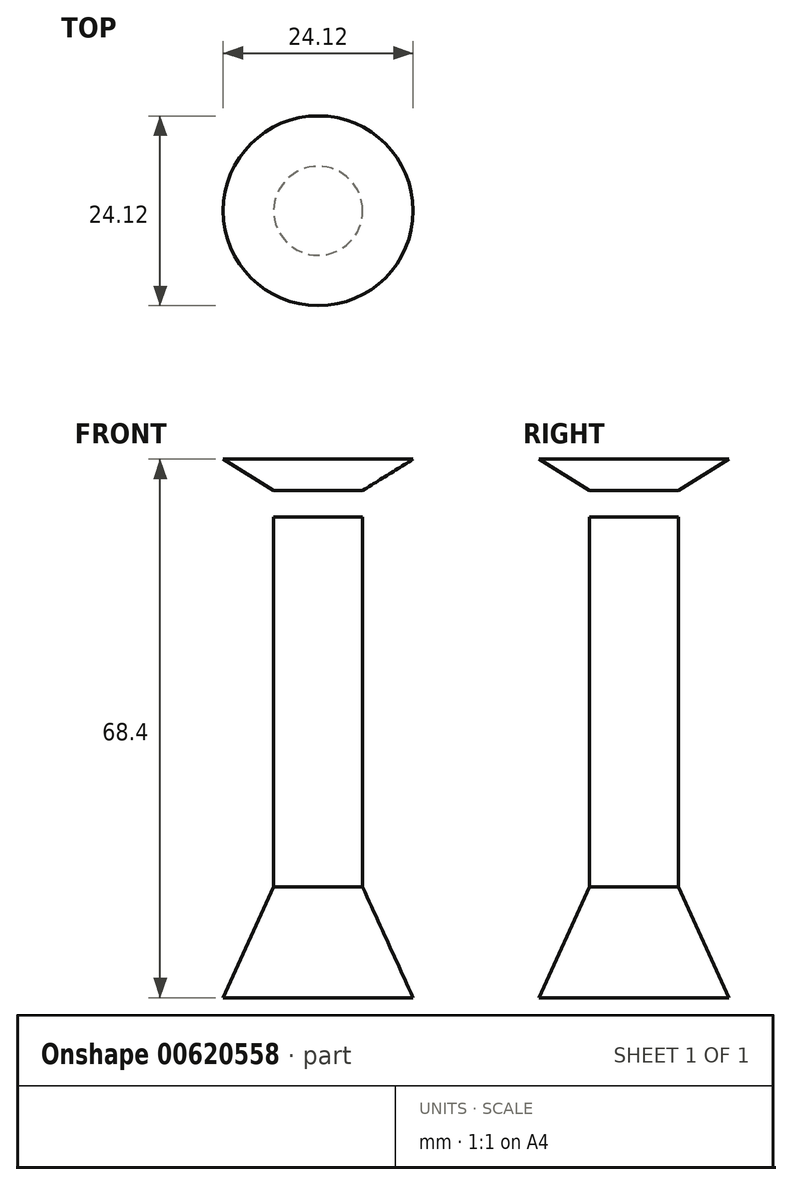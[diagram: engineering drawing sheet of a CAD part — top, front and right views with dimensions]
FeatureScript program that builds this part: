
annotation { "Feature Type Name" : "Feature", "Feature Type Description" : "" }
export const myFeature = defineFeature(function(context is Context, id is Id, definition is map)
    precondition{}
    {
        {
            var Q0;
            Q0=qCreatedBy(makeId("Front.planeOp"),FACE);
            var sketch = newSketch(context, id + "F0", { "sketchPlane" : qUnion([Q0])});
            skLineSegment(sketch, "E0.bottom", {"start": v(-5.65, 34.66) * mm, "end": v(0, 34.66) * mm});
            skLineSegment(sketch, "E0.top", {"start": v(-5.65, 30.7) * mm, "end": v(0, 30.7) * mm});
            skLineSegment(sketch, "E0.left", {"start": v(-5.65, 34.66) * mm, "end": v(-5.65, 30.7) * mm});
            skLineSegment(sketch, "E0.right", {"start": v(0, 34.66) * mm, "end": v(0, 30.7) * mm});
            skLineSegment(sketch, "E1.bottom", {"start": v(-2.82, 30.7) * mm, "end": v(0, 30.7) * mm});
            skLineSegment(sketch, "E1.top", {"start": v(-2.82, 27.33) * mm, "end": v(0, 27.33) * mm});
            skLineSegment(sketch, "E1.left", {"start": v(-2.82, 30.7) * mm, "end": v(-2.82, 27.33) * mm});
            skLineSegment(sketch, "E1.right", {"start": v(0, 30.7) * mm, "end": v(0, 27.33) * mm});
            skLineSegment(sketch, "E2.bottom", {"start": v(-5.65, 27.33) * mm, "end": v(0, 27.33) * mm});
            skLineSegment(sketch, "E2.top", {"start": v(-5.65, -19.7) * mm, "end": v(0, -19.7) * mm});
            skLineSegment(sketch, "E2.left", {"start": v(-5.65, 27.33) * mm, "end": v(-5.65, -19.7) * mm});
            skLineSegment(sketch, "E2.right", {"start": v(0, 27.33) * mm, "end": v(0, -19.7) * mm});
            skLineSegment(sketch, "E3", {"start": v(-5.65, 30.7) * mm, "end": v(-12.06, 34.66) * mm});
            skLineSegment(sketch, "E4", {"start": v(-12.06, 34.66) * mm, "end": v(-5.65, 34.66) * mm});
            skLineSegment(sketch, "E5", {"start": v(-5.65, -19.7) * mm, "end": v(-12.06, -33.74) * mm});
            skLineSegment(sketch, "E6", {"start": v(-12.06, -33.74) * mm, "end": v(0, -33.74) * mm});
            skLineSegment(sketch, "E7", {"start": v(0, -33.74) * mm, "end": v(0, -19.7) * mm});
            skSolve(sketch);
        }
        {
            var Q0;
            Q0=makeQuery(id+"F0.imprint","IMPRINT",FACE,{"disambiguationData":[TD([[makeQuery(id+"F0.imprint","IMPRINT",EDGE,{"derivedFrom":sQuery(id+"F0.wireOp",EDGE,"E0.bottom")}),-1.0]])]});
            var Q1;
            Q1=makeQuery(id+"F0.imprint","IMPRINT",FACE,{"disambiguationData":[TD([[makeQuery(id+"F0.imprint","IMPRINT",EDGE,{"derivedFrom":sQuery(id+"F0.wireOp",EDGE,"E0.left")}),-1.0]])]});
            var Q2;
            Q2=makeQuery(id+"F0.imprint","IMPRINT",FACE,{"disambiguationData":[TD([[makeQuery(id+"F0.imprint","IMPRINT",EDGE,{"derivedFrom":sQuery(id+"F0.wireOp",EDGE,"E2.top")}),1.0]])]});
            var Q3;
            Q3=makeQuery(id+"F0.imprint","IMPRINT",FACE,{"disambiguationData":[TD([[makeQuery(id+"F0.imprint","IMPRINT",EDGE,{"derivedFrom":sQuery(id+"F0.wireOp",EDGE,"E1.bottom")}),-1.0]])]});
            var Q4;
            Q4=makeQuery(id+"F0.imprint","IMPRINT",FACE,{"disambiguationData":[TD([[makeQuery(id+"F0.imprint","IMPRINT",EDGE,{"derivedFrom":sQuery(id+"F0.wireOp",EDGE,"E2.top")}),-1.0]])]});
            var Q5;
            Q5=sQuery(id+"F0.wireOp",EDGE,"E2.right");
            revolve(context, id + "F1", {"entities" : qUnion([Q0, Q1, Q2, Q3, Q4]), "axis" : qUnion([Q5]), "revolveType" : RevolveType.FULL});
        }
    });
